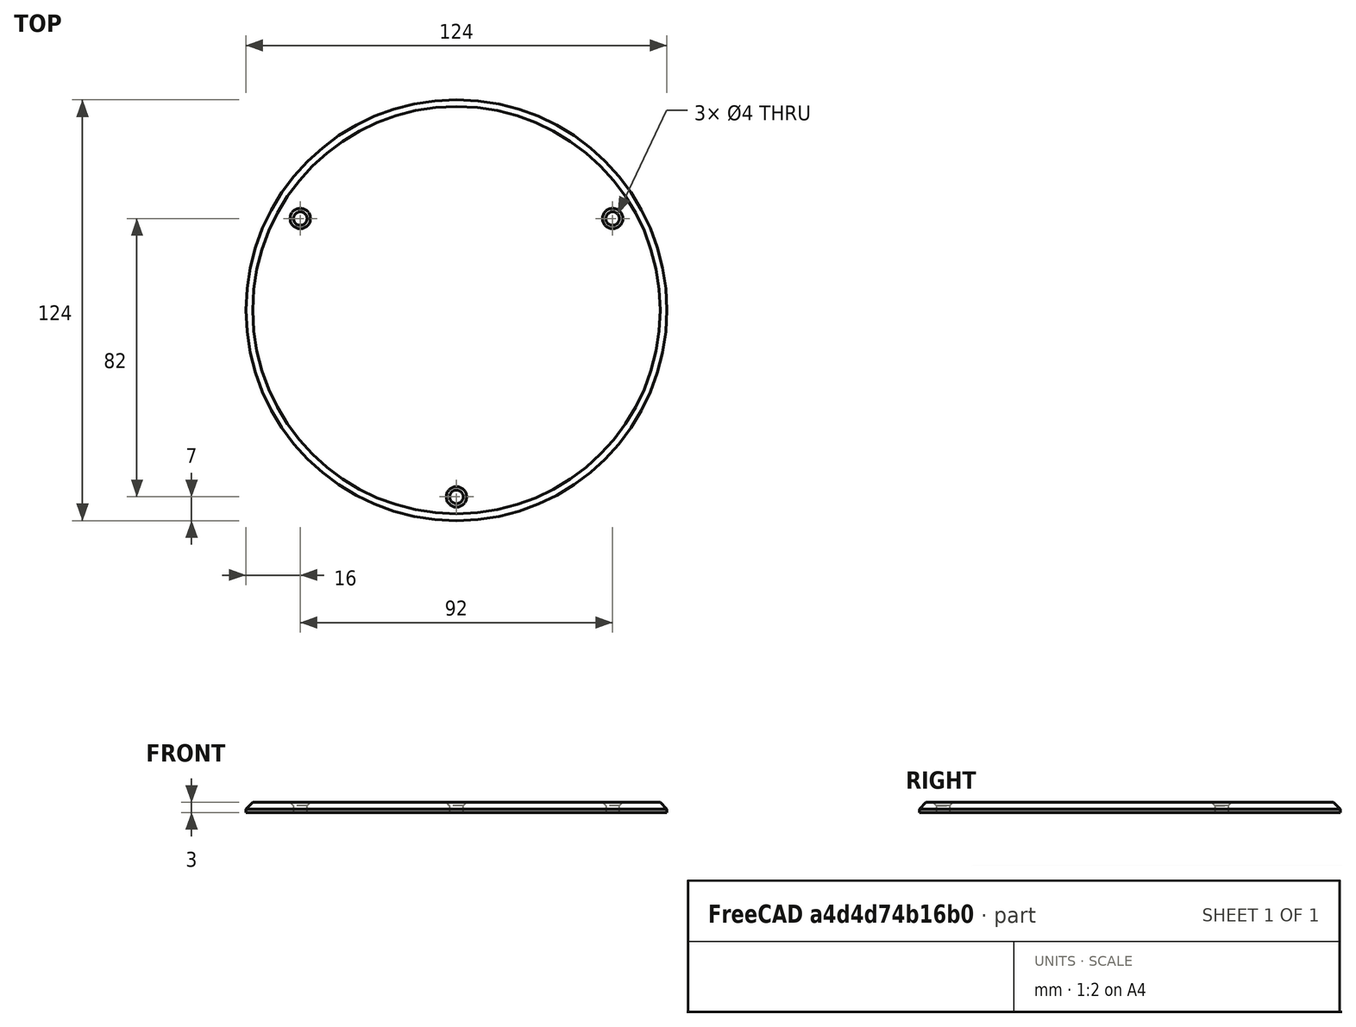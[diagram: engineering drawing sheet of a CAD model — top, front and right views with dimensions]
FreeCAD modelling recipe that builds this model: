
FCSTD DOCUMENT  (FreeCAD 0.21R33668 +26 (Git))
Label: compass
License: All rights reserved
LicenseURL: https://en.wikipedia.org/wiki/All_rights_reserved
objects: Part::Cylinder×4, Part::Chamfer×4, Part::Cut×3
note: 11 computed .brp shape members not serialized (recipe doc carries the construction recipe); baked Part::Feature solids carry a one-line shape summary decoded from their .brp

FEATURE [Part::Cylinder] Cylinder
  Angle = 360
  AttacherType = Attacher::AttachEngine3D
  FirstAngle = 0
  Height = 3
  Radius = 62
  SecondAngle = 0
FEATURE [Part::Cylinder] Cylinder001
  Angle = 360
  AttacherType = Attacher::AttachEngine3D
  FirstAngle = 0
  Height = 10
  Placement = pos=(0,-55,0) rot=(0,0,1;0rad)
  Radius = 2
  SecondAngle = 0
FEATURE [Part::Cylinder] Cylinder002
  Angle = 360
  AttacherType = Attacher::AttachEngine3D
  FirstAngle = 0
  Height = 10
  Placement = pos=(46,27,0) rot=(0,0,1;0rad)
  Radius = 2
  SecondAngle = 0
FEATURE [Part::Cylinder] Cylinder003
  Angle = 360
  AttacherType = Attacher::AttachEngine3D
  FirstAngle = 0
  Height = 10
  Placement = pos=(-46,27,0) rot=(0,0,1;0rad)
  Radius = 2
  SecondAngle = 0
FEATURE [Part::Cut] Cut
  Base = -> Cylinder
  Tool = -> Cylinder001
FEATURE [Part::Cut] Cut001
  Base = -> Cut
  Tool = -> Cylinder002
FEATURE [Part::Cut] Cut002
  Base = -> Cut001
  Tool = -> Cylinder003
FEATURE [Part::Chamfer] Chamfer
  Base = -> Cut002
  Edges = 1 edges r=2: [Edge3]
FEATURE [Part::Chamfer] Chamfer001
  Base = -> Chamfer
  Edges = 1 edges r=1: [Edge10]
FEATURE [Part::Chamfer] Chamfer002
  Base = -> Chamfer001
  Edges = 1 edges r=1: [Edge4]
FEATURE [Part::Chamfer] Chamfer003  label="cover-plate"
  Base = -> Chamfer002
  Edges = 1 edges r=1: [Edge4]
